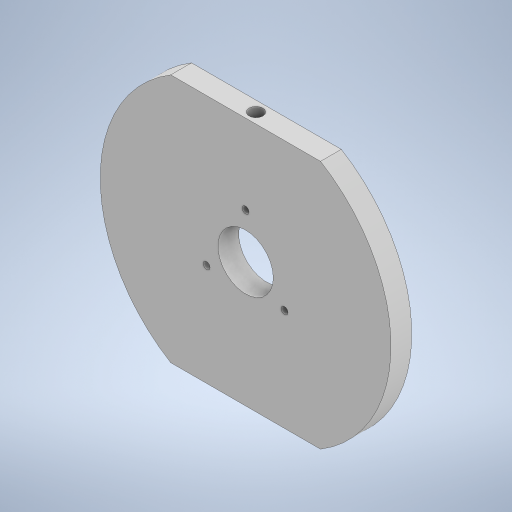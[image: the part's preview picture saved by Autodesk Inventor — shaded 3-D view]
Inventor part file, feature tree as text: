
AUTODESK INVENTOR PART (.ipt)
format: ipt  version: 2023 (Build 270158000, 158)  size: 247,296 bytes
history: native  units: in
note: dims shown in document units (in); Inventor stores cm internally (conversion verified against a paired STEP export)
features: extrude x2, sketch x2, other x1, plane x1, mirror x1
ambient origin geometry x8: Origin, YZ Plane, XZ Plane, XY Plane, X Axis, Y Axis, Z Axis, Center Point
bodies: Body1 (feature_tree)
feature tree (7):
  other  "Sólido1"
  extrude  "Extrusión1"  Depth=1.5748in
  extrude  "Extrusión2"  Depth=0.3937in
  plane  "Plano de trabajo1"
  mirror  "Simetría1"
  sketch  "Boceto1"  dims[d0=8.2677in d1=1.5748in]
  sketch  "Boceto2"  dims[d2=2.1654in d3=0.3937in d4=120.0deg d5=120.0deg d6=120.0deg d7=0.1969in d8=0.1969in d9=1.1811in d11=360.0deg d13=3.5433in d14=0.7874in d16=360.0deg d18=4.1339in d19=0.5906in d20=0.0in d21=0.3937in d22=0.7874in d23=0.0in]
